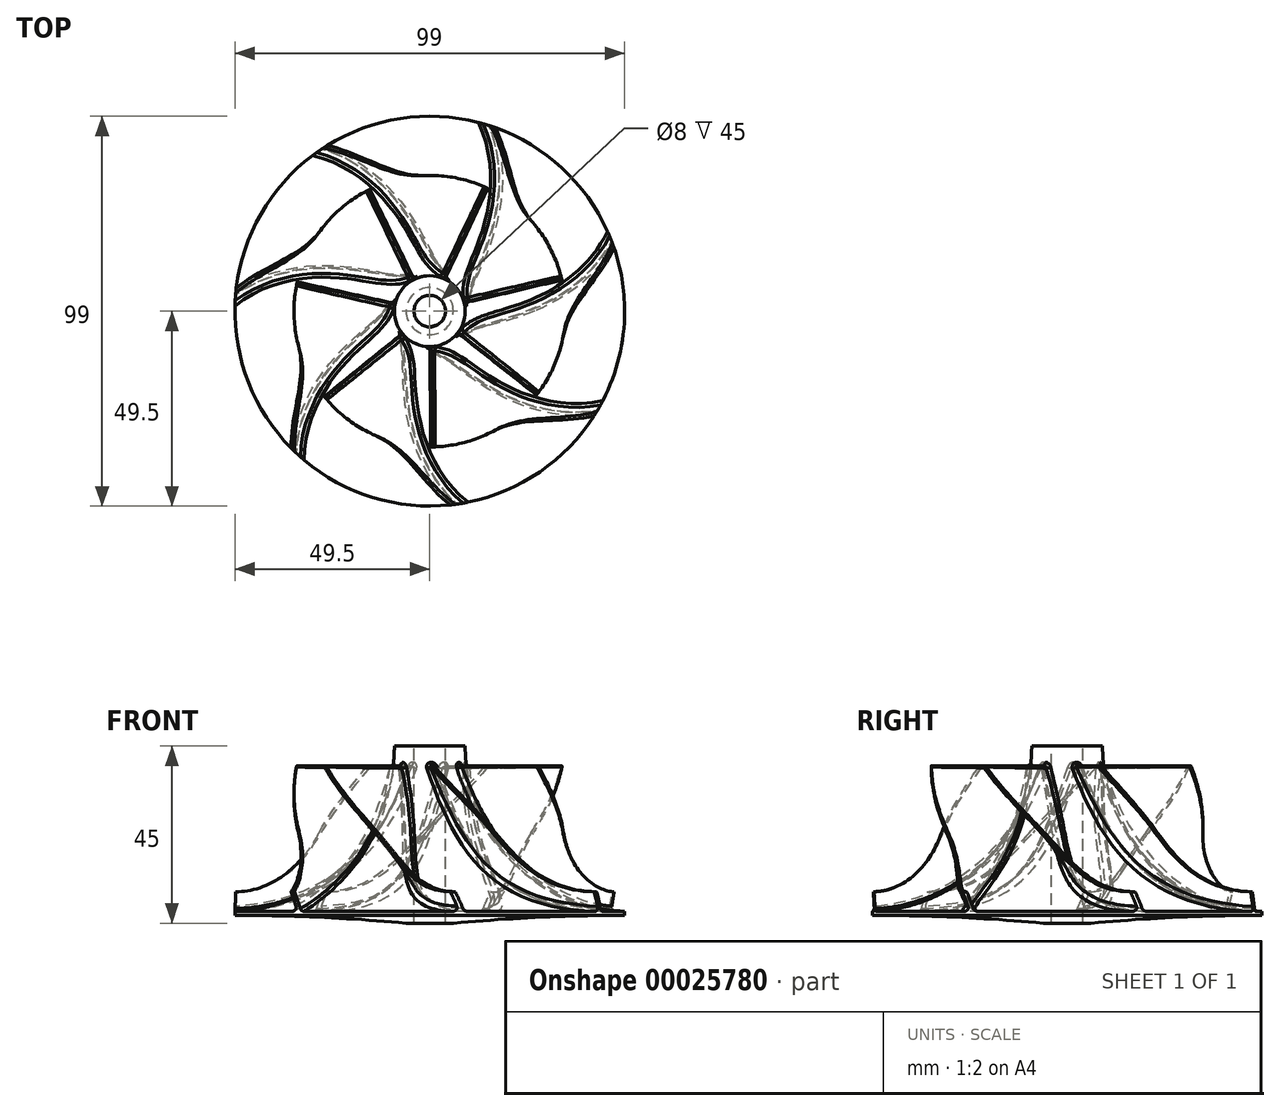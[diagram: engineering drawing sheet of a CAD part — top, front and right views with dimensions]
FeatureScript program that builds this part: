
annotation { "Feature Type Name" : "Feature", "Feature Type Description" : "" }
export const myFeature = defineFeature(function(context is Context, id is Id, definition is map)
    precondition{}
    {
        {
            var Q0;
            Q0=qCreatedBy(makeId("Front.planeOp"),FACE);
            var sketch = newSketch(context, id + "F0", { "sketchPlane" : qUnion([Q0])});
            skLineSegment(sketch, "E0", {"start": v(-4, 0) * mm, "end": v(-4, 45) * mm});
            skLineSegment(sketch, "E1", {"start": v(-4, 0) * mm, "end": v(-6, 0) * mm});
            skLineSegment(sketch, "E2", {"start": v(-6, 0) * mm, "end": v(-6, 2) * mm, "construction": true});
            skLineSegment(sketch, "E3", {"start": v(-6, 2) * mm, "end": v(-49.5, 2) * mm, "construction": true});
            skLineSegment(sketch, "E4", {"start": v(-49.5, 2) * mm, "end": v(-49.5, 3) * mm});
            skLineSegment(sketch, "E5", {"start": v(-4, 45) * mm, "end": v(-9, 45) * mm});
            skLineSegment(sketch, "E6", {"start": v(0, 58.9) * mm, "end": v(0, -58.23) * mm, "construction": true});
            skArc(sketch, "E7", {"start": v(-9, 45) * mm, "mid": v(-20.77, 15.82) * mm, "end": v(-49.5, 3) * mm});
            skArc(sketch, "E8", {"start": v(-6, 0) * mm, "mid": v(-27.73, 1.5) * mm, "end": v(-49.5, 2) * mm});
            skSolve(sketch);
        }
        {
            var Q0;
            Q0 = qSketchRegion(id + "F0", true);
            var Q1;
            Q1=sQuery(id+"F0.wireOp",EDGE,"E6");
            revolve(context, id + "F1", {"entities" : qUnion([Q0]), "axis" : qUnion([Q1]), "revolveType" : RevolveType.FULL});
        }
        {
            var Q0;
            Q0=qCreatedBy(makeId("Top.planeOp"),FACE);
            cPlane(context, id + "F2", {"entities" : qUnion([Q0]), "cplaneType" : CPlaneType.OFFSET, "offset" : 40 * mm, "width" : 150 * mm, "height" : 150 * mm});
        }
        {
            var Q0;
            Q0=qCreatedBy(makeId("Top.planeOp"),FACE);
            cPlane(context, id + "F3", {"entities" : qUnion([Q0]), "cplaneType" : CPlaneType.OFFSET, "offset" : 3 * mm, "width" : 150 * mm, "height" : 150 * mm});
        }
        {
            var Q0;
            Q0=qCreatedBy(id+"F2.planeOp",FACE);
            var sketch = newSketch(context, id + "F4", { "sketchPlane" : qUnion([Q0])});
            skArc(sketch, "E9.0", {"start": v(0, -49.5) * mm, "mid": v(0.5, -49.5) * mm, "end": v(1, -49.49) * mm});
            skLineSegment(sketch, "E10", {"start": v(0, -4) * mm, "end": v(0, -49.5) * mm});
            skLineSegment(sketch, "E11.0", {"start": v(1, -4) * mm, "end": v(1, -49.5) * mm});
            skLineSegment(sketch, "E12", {"start": v(0, -4) * mm, "end": v(1, -4) * mm});
            skSolve(sketch);
        }
        {
            var Q0;
            Q0=qCreatedBy(id+"F3.planeOp",FACE);
            var sketch = newSketch(context, id + "F5", { "sketchPlane" : qUnion([Q0])});
            skLineSegment(sketch, "E13", {"start": v(39, 4.4) * mm, "end": v(39, 0) * mm});
            skLineSegment(sketch, "E14", {"start": v(0, 0) * mm, "end": v(14, 0) * mm, "construction": true});
            skLineSegment(sketch, "E15", {"start": v(14, 0) * mm, "end": v(14, 4.4) * mm, "construction": true});
            skCircle(sketch, "E16.0", {"center": v(0, 0) * mm, "radius": 49.5 * mm, "construction": true});
            skLineSegment(sketch, "E17", {"start": v(0, 0) * mm, "end": v(42.87, -24.75) * mm, "construction": true});
            skArc(sketch, "E18", {"start": v(14, 0) * mm, "mid": v(25.54, -21.07) * mm, "end": v(49.5, -22.69) * mm});
            skLineSegment(sketch, "E19", {"start": v(49.5, -21.58) * mm, "end": v(49.5, -22.69) * mm});
            skArc(sketch, "E20.0", {"start": v(15, 0) * mm, "mid": v(26.27, -20.35) * mm, "end": v(49.5, -21.58) * mm});
            skPoint(sketch, "E21.orphan", {"position": v(49.5, 0) * mm});
            skLineSegment(sketch, "E22", {"start": v(14, 0) * mm, "end": v(15, 0) * mm});
            skSolve(sketch);
        }
        {
            var Q1;
            Q1 = qSketchRegion(id + "F4", true);
            var Q2;
            Q2 = qSketchRegion(id + "F5", true);
            loft(context, id + "F6", {"operationType" : NewBodyOperationType.ADD, "sheetProfilesArray" : [{ "sheetProfileEntities" : qUnion([Q1]) }, { "sheetProfileEntities" : qUnion([Q2]) }]});
        }
        {
            var Q0;
            Q0=qCreatedBy(makeId("Front.planeOp"),FACE);
            var sketch = newSketch(context, id + "F7", { "sketchPlane" : qUnion([Q0])});
            skPoint(sketch, "E23.0", {"position": v(0, 40) * mm});
            skLineSegment(sketch, "E24", {"start": v(0, 40) * mm, "end": v(-9.3, 40) * mm});
            skPoint(sketch, "E25", {"position": v(-34.5, 40) * mm});
            skLineSegment(sketch, "E26", {"start": v(0, 61.5) * mm, "end": v(0, -16.06) * mm, "construction": true});
            skLineSegment(sketch, "E27", {"start": v(-34.5, 40) * mm, "end": v(-34.5, 23) * mm});
            skLineSegment(sketch, "E28", {"start": v(-49.5, 8) * mm, "end": v(-64.35, 8) * mm, "construction": true});
            skLineSegment(sketch, "E29", {"start": v(-49.5, 8) * mm, "end": v(-49.5, 23) * mm, "construction": true});
            skArc(sketch, "E30", {"start": v(-49.5, 3) * mm, "mid": v(-20.77, 15.82) * mm, "end": v(-9, 45) * mm, "construction": true});
            skArc(sketch, "E31", {"start": v(-49.5, 8) * mm, "mid": v(-38.9, 12.4) * mm, "end": v(-34.5, 23) * mm});
            skLineSegment(sketch, "E32.trimOffspring", {"start": v(-34.5, 40) * mm, "end": v(-69.01, 40) * mm});
            skLineSegment(sketch, "E33", {"start": v(-49.5, 8) * mm, "end": v(-49.5, 3) * mm});
            skLineSegment(sketch, "E34", {"start": v(-49.5, 3) * mm, "end": v(-69.01, 3) * mm});
            skLineSegment(sketch, "E35", {"start": v(-69.01, 3) * mm, "end": v(-69.01, 40) * mm});
            skSolve(sketch);
        }
        {
            var Q0;
            Q0 = qSketchRegion(id + "F7", true);
            var Q1;
            Q1=sQuery(id+"F7.wireOp",EDGE,"E26");
            revolve(context, id + "F8", {"operationType" : NewBodyOperationType.REMOVE, "entities" : qUnion([Q0]), "axis" : qUnion([Q1]), "revolveType" : RevolveType.FULL, "oppositeDirection" : true});
        }
        {
            var Q0;
            Q0=makeQuery(id+"F6.opLoft","SWEPT_FACE",FACE,{"disambiguationData":[OSD([sQuery(id+"F4.wireOp",EDGE,"E9.0"),sQuery(id+"F4.wireOp",EDGE,"E11.0"),sQuery(id+"F4.wireOp",EDGE,"E12"),sQuery(id+"F5.wireOp",EDGE,"E19"),sQuery(id+"F5.wireOp",EDGE,"E20.0"),sQuery(id+"F5.wireOp",EDGE,"E22")])]});
            var Q1;
            Q1=makeQuery(id+"F8.boolean.opBoolean","COPY",FACE,{"derivedFrom":makeQuery(id+"F8.opRevolve","SWEPT_FACE",FACE,{"disambiguationData":[OSD([sQuery(id+"F7.wireOp",EDGE,"E31")])]})});
            var Q2;
            Q2=makeQuery(id+"F8.boolean.opBoolean","COPY",FACE,{"derivedFrom":makeQuery(id+"F8.opRevolve","SWEPT_FACE",FACE,{"disambiguationData":[OSD([sQuery(id+"F7.wireOp",EDGE,"E27")])]})});
            var Q3;
            {var subQ0=sQuery(id+"F4.wireOp",EDGE,"E9.0");var subQ1=sQuery(id+"F4.wireOp",EDGE,"E10");var subQ2=sQuery(id+"F4.wireOp",EDGE,"E12");var subQ3=sQuery(id+"F5.wireOp",EDGE,"E18");var subQ4=sQuery(id+"F5.wireOp",EDGE,"E19");var subQ5=sQuery(id+"F5.wireOp",EDGE,"E22");Q3=makeQuery(id+"F6.boolean.opBoolean","SPLIT",FACE,{"disambiguationData":[TD([makeQuery(id+"F1.opRevolve","SWEPT_FACE",FACE,{"disambiguationData":[OSD([sQuery(id+"F0.wireOp",EDGE,"E4")])]})])],"derivedFrom":makeQuery(id+"F6.opLoft","SWEPT_FACE",FACE,{"disambiguationData":[OSD([subQ0,subQ1,subQ2,subQ3,subQ4,subQ5])]})});}
            var Q4;
            {var subQ2=sQuery(id+"F4.wireOp",EDGE,"E9.0");Q4=makeQuery(id+"F6.opLoft","CAP_FACE",FACE,{"disambiguationData":[OSD([makeQuery(id+"F4.imprint","IMPRINT",FACE,{"disambiguationData":[TD([[makeQuery(id+"F4.imprint","IMPRINT",EDGE,{"derivedFrom":subQ2}),1.0]])]})])],"isStart":true});}
            var Q5;
            Q5=makeQuery(id+"F1.opRevolve","SWEPT_FACE",FACE,{"disambiguationData":[OSD([sQuery(id+"F0.wireOp",EDGE,"E0")])]});
            circularPattern(context, id + "F9", {"faces" : qUnion([Q0, Q1, Q2, Q3, Q4]), "axis" : qUnion([Q5]), "angle" : 51.43 * degree, "instanceCount" : 7, "patternType" : PatternType.FACE});
        }
        {
            var Q0;
            Q0=makeQuery(id+"F6.opLoft","MID_CAP_EDGE",EDGE,{"disambiguationData":[OSD([sQuery(id+"F4.wireOp",EDGE,"E9.0"),sQuery(id+"F4.wireOp",EDGE,"E10"),sQuery(id+"F4.wireOp",EDGE,"E12")])],"capPos":0.0});
            var Q1;
            Q1=makeQuery(id+"F9.opPattern","COPY",EDGE,{"derivedFrom":makeQuery(id+"F6.opLoft","MID_CAP_EDGE",EDGE,{"disambiguationData":[OSD([sQuery(id+"F4.wireOp",EDGE,"E9.0"),sQuery(id+"F4.wireOp",EDGE,"E10"),sQuery(id+"F4.wireOp",EDGE,"E12")])],"capPos":0.0}),"instanceName":"1"});
            var Q2;
            Q2=makeQuery(id+"F9.opPattern","COPY",EDGE,{"derivedFrom":makeQuery(id+"F6.opLoft","MID_CAP_EDGE",EDGE,{"disambiguationData":[OSD([sQuery(id+"F4.wireOp",EDGE,"E9.0"),sQuery(id+"F4.wireOp",EDGE,"E10"),sQuery(id+"F4.wireOp",EDGE,"E12")])],"capPos":0.0}),"instanceName":"6"});
            var Q3;
            Q3=makeQuery(id+"F9.opPattern","COPY",EDGE,{"derivedFrom":makeQuery(id+"F6.opLoft","MID_CAP_EDGE",EDGE,{"disambiguationData":[OSD([sQuery(id+"F4.wireOp",EDGE,"E9.0"),sQuery(id+"F4.wireOp",EDGE,"E10"),sQuery(id+"F4.wireOp",EDGE,"E12")])],"capPos":0.0}),"instanceName":"5"});
            var Q4;
            Q4=makeQuery(id+"F9.opPattern","COPY",EDGE,{"derivedFrom":makeQuery(id+"F6.opLoft","MID_CAP_EDGE",EDGE,{"disambiguationData":[OSD([sQuery(id+"F4.wireOp",EDGE,"E9.0"),sQuery(id+"F4.wireOp",EDGE,"E10"),sQuery(id+"F4.wireOp",EDGE,"E12")])],"capPos":0.0}),"instanceName":"4"});
            var Q5;
            Q5=makeQuery(id+"F9.opPattern","COPY",EDGE,{"derivedFrom":makeQuery(id+"F6.opLoft","MID_CAP_EDGE",EDGE,{"disambiguationData":[OSD([sQuery(id+"F4.wireOp",EDGE,"E9.0"),sQuery(id+"F4.wireOp",EDGE,"E10"),sQuery(id+"F4.wireOp",EDGE,"E12")])],"capPos":0.0}),"instanceName":"3"});
            var Q6;
            Q6=makeQuery(id+"F9.opPattern","COPY",EDGE,{"derivedFrom":makeQuery(id+"F6.opLoft","MID_CAP_EDGE",EDGE,{"disambiguationData":[OSD([sQuery(id+"F4.wireOp",EDGE,"E9.0"),sQuery(id+"F4.wireOp",EDGE,"E10"),sQuery(id+"F4.wireOp",EDGE,"E12")])],"capPos":0.0}),"instanceName":"2"});
            fillet(context, id + "F10", {"entities" : qUnion([Q0, Q1, Q2, Q3, Q4, Q5, Q6]), "radius" : .2 * mm, "tangentPropagation" : true, "allowEdgeOverflow" : false});
        }
        {
            var Q0;
            Q0=makeQuery(id+"F9.opPattern","COPY",EDGE,{"derivedFrom":makeQuery(id+"F6.opLoft","MID_CAP_EDGE",EDGE,{"disambiguationData":[OSD([sQuery(id+"F4.wireOp",EDGE,"E9.0"),sQuery(id+"F4.wireOp",EDGE,"E11.0"),sQuery(id+"F4.wireOp",EDGE,"E12")])],"capPos":0.0}),"instanceName":"2"});
            var Q1;
            Q1=makeQuery(id+"F9.opPattern","COPY",EDGE,{"derivedFrom":makeQuery(id+"F6.opLoft","MID_CAP_EDGE",EDGE,{"disambiguationData":[OSD([sQuery(id+"F4.wireOp",EDGE,"E9.0"),sQuery(id+"F4.wireOp",EDGE,"E11.0"),sQuery(id+"F4.wireOp",EDGE,"E12")])],"capPos":0.0}),"instanceName":"1"});
            var Q2;
            Q2=makeQuery(id+"F6.opLoft","MID_CAP_EDGE",EDGE,{"disambiguationData":[OSD([sQuery(id+"F4.wireOp",EDGE,"E9.0"),sQuery(id+"F4.wireOp",EDGE,"E11.0"),sQuery(id+"F4.wireOp",EDGE,"E12")])],"capPos":0.0});
            var Q3;
            Q3=makeQuery(id+"F9.opPattern","COPY",EDGE,{"derivedFrom":makeQuery(id+"F6.opLoft","MID_CAP_EDGE",EDGE,{"disambiguationData":[OSD([sQuery(id+"F4.wireOp",EDGE,"E9.0"),sQuery(id+"F4.wireOp",EDGE,"E11.0"),sQuery(id+"F4.wireOp",EDGE,"E12")])],"capPos":0.0}),"instanceName":"6"});
            var Q4;
            Q4=makeQuery(id+"F9.opPattern","COPY",EDGE,{"derivedFrom":makeQuery(id+"F6.opLoft","MID_CAP_EDGE",EDGE,{"disambiguationData":[OSD([sQuery(id+"F4.wireOp",EDGE,"E9.0"),sQuery(id+"F4.wireOp",EDGE,"E11.0"),sQuery(id+"F4.wireOp",EDGE,"E12")])],"capPos":0.0}),"instanceName":"5"});
            var Q5;
            Q5=makeQuery(id+"F9.opPattern","COPY",EDGE,{"derivedFrom":makeQuery(id+"F6.opLoft","MID_CAP_EDGE",EDGE,{"disambiguationData":[OSD([sQuery(id+"F4.wireOp",EDGE,"E9.0"),sQuery(id+"F4.wireOp",EDGE,"E11.0"),sQuery(id+"F4.wireOp",EDGE,"E12")])],"capPos":0.0}),"instanceName":"4"});
            var Q6;
            Q6=makeQuery(id+"F9.opPattern","COPY",EDGE,{"derivedFrom":makeQuery(id+"F6.opLoft","MID_CAP_EDGE",EDGE,{"disambiguationData":[OSD([sQuery(id+"F4.wireOp",EDGE,"E9.0"),sQuery(id+"F4.wireOp",EDGE,"E11.0"),sQuery(id+"F4.wireOp",EDGE,"E12")])],"capPos":0.0}),"instanceName":"3"});
            fillet(context, id + "F11", {"entities" : qUnion([Q0, Q1, Q2, Q3, Q4, Q5, Q6]), "radius" : 1 * mm, "tangentPropagation" : true, "allowEdgeOverflow" : false});
        }
        {
            var Q0;
            Q0=makeQuery(id+"F9.opPattern","COPY",EDGE,{"derivedFrom":makeQuery(id+"F6.boolean.opBoolean","INTERSECT",EDGE,{"derivedFrom":[makeQuery(id+"F1.opRevolve","SWEPT_FACE",FACE,{"disambiguationData":[OSD([sQuery(id+"F0.wireOp",EDGE,"E7")])]}),makeQuery(id+"F6.opLoft","SWEPT_FACE",FACE,{"disambiguationData":[OSD([sQuery(id+"F4.wireOp",EDGE,"E9.0"),sQuery(id+"F4.wireOp",EDGE,"E10"),sQuery(id+"F4.wireOp",EDGE,"E12"),sQuery(id+"F5.wireOp",EDGE,"E18"),sQuery(id+"F5.wireOp",EDGE,"E19"),sQuery(id+"F5.wireOp",EDGE,"E22")])]})]}),"instanceName":"2"});
            var Q1;
            Q1=makeQuery(id+"F10.opFillet","BLEND_EDGE",EDGE,{"blendedFrom":[makeQuery(id+"F9.opPattern","COPY",EDGE,{"derivedFrom":makeQuery(id+"F6.opLoft","MID_CAP_EDGE",EDGE,{"disambiguationData":[OSD([sQuery(id+"F4.wireOp",EDGE,"E9.0"),sQuery(id+"F4.wireOp",EDGE,"E10"),sQuery(id+"F4.wireOp",EDGE,"E12")])],"capPos":0.0}),"instanceName":"2"}),makeQuery(id+"F1.opRevolve","SWEPT_FACE",FACE,{"disambiguationData":[OSD([sQuery(id+"F0.wireOp",EDGE,"E7")])]})],"blendedInto":[makeQuery(id+"F1.opRevolve","SWEPT_FACE",FACE,{"disambiguationData":[OSD([sQuery(id+"F0.wireOp",EDGE,"E7")])]})]});
            var Q2;
            {var subQ2=sQuery(id+"F4.wireOp",EDGE,"E9.0");Q2=makeQuery(id+"F9.opPattern","COPY",EDGE,{"derivedFrom":makeQuery(id+"F6.boolean.opBoolean","INTERSECT",EDGE,{"derivedFrom":[makeQuery(id+"F1.opRevolve","SWEPT_FACE",FACE,{"disambiguationData":[OSD([sQuery(id+"F0.wireOp",EDGE,"E7")])]}),makeQuery(id+"F6.opLoft","CAP_FACE",FACE,{"disambiguationData":[OSD([makeQuery(id+"F4.imprint","IMPRINT",FACE,{"disambiguationData":[TD([[makeQuery(id+"F4.imprint","IMPRINT",EDGE,{"derivedFrom":subQ2}),1.0]])]})])],"isStart":true})]}),"instanceName":"2"});}
            var Q3;
            Q3=makeQuery(id+"F11.opFillet","BLEND_EDGE",EDGE,{"blendedFrom":[makeQuery(id+"F9.opPattern","COPY",EDGE,{"derivedFrom":makeQuery(id+"F6.opLoft","MID_CAP_EDGE",EDGE,{"disambiguationData":[OSD([sQuery(id+"F4.wireOp",EDGE,"E9.0"),sQuery(id+"F4.wireOp",EDGE,"E11.0"),sQuery(id+"F4.wireOp",EDGE,"E12")])],"capPos":0.0}),"instanceName":"2"}),makeQuery(id+"F1.opRevolve","SWEPT_FACE",FACE,{"disambiguationData":[OSD([sQuery(id+"F0.wireOp",EDGE,"E7")])]})],"blendedInto":[makeQuery(id+"F1.opRevolve","SWEPT_FACE",FACE,{"disambiguationData":[OSD([sQuery(id+"F0.wireOp",EDGE,"E7")])]})]});
            var Q4;
            Q4=makeQuery(id+"F9.opPattern","COPY",EDGE,{"derivedFrom":makeQuery(id+"F6.boolean.opBoolean","INTERSECT",EDGE,{"derivedFrom":[makeQuery(id+"F1.opRevolve","SWEPT_FACE",FACE,{"disambiguationData":[OSD([sQuery(id+"F0.wireOp",EDGE,"E7")])]}),makeQuery(id+"F6.opLoft","SWEPT_FACE",FACE,{"disambiguationData":[OSD([sQuery(id+"F4.wireOp",EDGE,"E9.0"),sQuery(id+"F4.wireOp",EDGE,"E11.0"),sQuery(id+"F4.wireOp",EDGE,"E12"),sQuery(id+"F5.wireOp",EDGE,"E19"),sQuery(id+"F5.wireOp",EDGE,"E20.0"),sQuery(id+"F5.wireOp",EDGE,"E22")])]})]}),"instanceName":"2"});
            var Q5;
            Q5=makeQuery(id+"F9.opPattern","COPY",EDGE,{"derivedFrom":makeQuery(id+"F6.boolean.opBoolean","INTERSECT",EDGE,{"derivedFrom":[makeQuery(id+"F1.opRevolve","SWEPT_FACE",FACE,{"disambiguationData":[OSD([sQuery(id+"F0.wireOp",EDGE,"E7")])]}),makeQuery(id+"F6.opLoft","SWEPT_FACE",FACE,{"disambiguationData":[OSD([sQuery(id+"F4.wireOp",EDGE,"E9.0"),sQuery(id+"F4.wireOp",EDGE,"E10"),sQuery(id+"F4.wireOp",EDGE,"E12"),sQuery(id+"F5.wireOp",EDGE,"E18"),sQuery(id+"F5.wireOp",EDGE,"E19"),sQuery(id+"F5.wireOp",EDGE,"E22")])]})]}),"instanceName":"1"});
            var Q6;
            Q6=makeQuery(id+"F6.boolean.opBoolean","INTERSECT",EDGE,{"derivedFrom":[makeQuery(id+"F1.opRevolve","SWEPT_FACE",FACE,{"disambiguationData":[OSD([sQuery(id+"F0.wireOp",EDGE,"E7")])]}),makeQuery(id+"F6.opLoft","SWEPT_FACE",FACE,{"disambiguationData":[OSD([sQuery(id+"F4.wireOp",EDGE,"E9.0"),sQuery(id+"F4.wireOp",EDGE,"E10"),sQuery(id+"F4.wireOp",EDGE,"E12"),sQuery(id+"F5.wireOp",EDGE,"E18"),sQuery(id+"F5.wireOp",EDGE,"E19"),sQuery(id+"F5.wireOp",EDGE,"E22")])]})]});
            var Q7;
            Q7=makeQuery(id+"F9.opPattern","COPY",EDGE,{"derivedFrom":makeQuery(id+"F6.boolean.opBoolean","INTERSECT",EDGE,{"derivedFrom":[makeQuery(id+"F1.opRevolve","SWEPT_FACE",FACE,{"disambiguationData":[OSD([sQuery(id+"F0.wireOp",EDGE,"E7")])]}),makeQuery(id+"F6.opLoft","SWEPT_FACE",FACE,{"disambiguationData":[OSD([sQuery(id+"F4.wireOp",EDGE,"E9.0"),sQuery(id+"F4.wireOp",EDGE,"E10"),sQuery(id+"F4.wireOp",EDGE,"E12"),sQuery(id+"F5.wireOp",EDGE,"E18"),sQuery(id+"F5.wireOp",EDGE,"E19"),sQuery(id+"F5.wireOp",EDGE,"E22")])]})]}),"instanceName":"6"});
            var Q8;
            Q8=makeQuery(id+"F9.opPattern","COPY",EDGE,{"derivedFrom":makeQuery(id+"F6.boolean.opBoolean","INTERSECT",EDGE,{"derivedFrom":[makeQuery(id+"F1.opRevolve","SWEPT_FACE",FACE,{"disambiguationData":[OSD([sQuery(id+"F0.wireOp",EDGE,"E7")])]}),makeQuery(id+"F6.opLoft","SWEPT_FACE",FACE,{"disambiguationData":[OSD([sQuery(id+"F4.wireOp",EDGE,"E9.0"),sQuery(id+"F4.wireOp",EDGE,"E10"),sQuery(id+"F4.wireOp",EDGE,"E12"),sQuery(id+"F5.wireOp",EDGE,"E18"),sQuery(id+"F5.wireOp",EDGE,"E19"),sQuery(id+"F5.wireOp",EDGE,"E22")])]})]}),"instanceName":"5"});
            var Q9;
            Q9=makeQuery(id+"F9.opPattern","COPY",EDGE,{"derivedFrom":makeQuery(id+"F6.boolean.opBoolean","INTERSECT",EDGE,{"derivedFrom":[makeQuery(id+"F1.opRevolve","SWEPT_FACE",FACE,{"disambiguationData":[OSD([sQuery(id+"F0.wireOp",EDGE,"E7")])]}),makeQuery(id+"F6.opLoft","SWEPT_FACE",FACE,{"disambiguationData":[OSD([sQuery(id+"F4.wireOp",EDGE,"E9.0"),sQuery(id+"F4.wireOp",EDGE,"E10"),sQuery(id+"F4.wireOp",EDGE,"E12"),sQuery(id+"F5.wireOp",EDGE,"E18"),sQuery(id+"F5.wireOp",EDGE,"E19"),sQuery(id+"F5.wireOp",EDGE,"E22")])]})]}),"instanceName":"4"});
            var Q10;
            Q10=makeQuery(id+"F9.opPattern","COPY",EDGE,{"derivedFrom":makeQuery(id+"F6.boolean.opBoolean","INTERSECT",EDGE,{"derivedFrom":[makeQuery(id+"F1.opRevolve","SWEPT_FACE",FACE,{"disambiguationData":[OSD([sQuery(id+"F0.wireOp",EDGE,"E7")])]}),makeQuery(id+"F6.opLoft","SWEPT_FACE",FACE,{"disambiguationData":[OSD([sQuery(id+"F4.wireOp",EDGE,"E9.0"),sQuery(id+"F4.wireOp",EDGE,"E10"),sQuery(id+"F4.wireOp",EDGE,"E12"),sQuery(id+"F5.wireOp",EDGE,"E18"),sQuery(id+"F5.wireOp",EDGE,"E19"),sQuery(id+"F5.wireOp",EDGE,"E22")])]})]}),"instanceName":"3"});
            fillet(context, id + "F12", {"entities" : qUnion([Q0, Q1, Q2, Q3, Q4, Q5, Q6, Q7, Q8, Q9, Q10]), "radius" : 1 * mm, "tangentPropagation" : true, "allowEdgeOverflow" : false});
        }
    });
